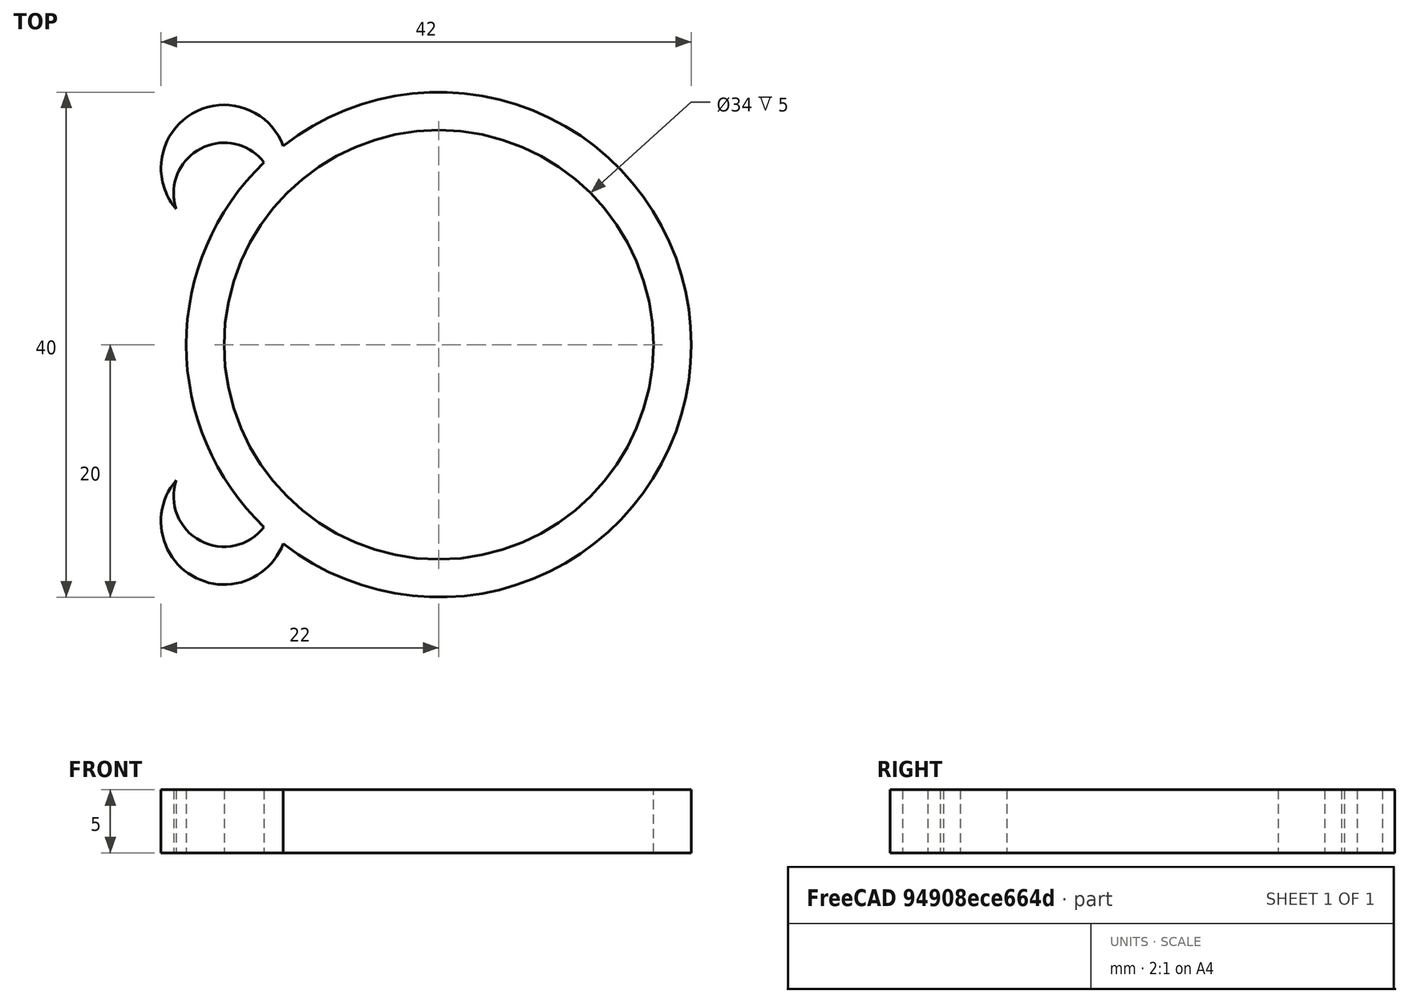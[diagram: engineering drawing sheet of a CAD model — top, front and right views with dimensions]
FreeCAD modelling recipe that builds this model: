
FCSTD DOCUMENT  (FreeCAD 0.20R29410 (Git))
Label: demon
License: Creative Commons Attribution
LicenseURL: http://creativecommons.org/licenses/by/4.0/
objects: Part::Cylinder×6, Part::Cut×3, Part::MultiFuse×2
note: 11 computed .brp shape members not serialized (recipe doc carries the construction recipe); baked Part::Feature solids carry a one-line shape summary decoded from their .brp

FEATURE [Part::Cylinder] Cylinder  label="Cilindro"
  Angle = 360
  AttacherType = Attacher::AttachEngine3D
  FirstAngle = 0
  Height = 5
  Radius = 20
  SecondAngle = 0
FEATURE [Part::Cylinder] Cylinder001  label="Cilindro001"
  Angle = 360
  AttacherType = Attacher::AttachEngine3D
  FirstAngle = 0
  Height = 5
  Radius = 17
  SecondAngle = 0
FEATURE [Part::Cut] Cut
  Base = -> Cylinder
  Refine = true
  Tool = -> Cylinder001
FEATURE [Part::Cylinder] Cylinder002  label="Cilindro002"
  Angle = 360
  AttacherType = Attacher::AttachEngine3D
  FirstAngle = 0
  Height = 5
  Radius = 5
  SecondAngle = 0
FEATURE [Part::Cylinder] Cylinder003  label="Cilindro003"
  Angle = 360
  AttacherType = Attacher::AttachEngine3D
  FirstAngle = 0
  Height = 5
  Placement = pos=(0,2,0) rot=(0,0,1;0rad)
  Radius = 4
  SecondAngle = 0
FEATURE [Part::Cut] Cut001
  Base = -> Cylinder002
  Placement = pos=(-17,-14,0) rot=(0,0,1;0rad)
  Refine = true
  Tool = -> Cylinder003
FEATURE [Part::Cylinder] Cylinder004  label="Cilindro004"
  Angle = 360
  AttacherType = Attacher::AttachEngine3D
  FirstAngle = 0
  Height = 5
  Radius = 5
  SecondAngle = 0
FEATURE [Part::Cylinder] Cylinder005  label="Cilindro005"
  Angle = 360
  AttacherType = Attacher::AttachEngine3D
  FirstAngle = 0
  Height = 5
  Placement = pos=(0,2,0) rot=(0,0,1;0rad)
  Radius = 4
  SecondAngle = 0
FEATURE [Part::Cut] Cut002
  Base = -> Cylinder004
  Placement = pos=(-17,14,0) rot=(0,0,-1;3.14159rad)
  Refine = true
  Tool = -> Cylinder005
FEATURE [Part::MultiFuse] Fusion
  Refine = true
  Shapes = -> [Cut,Cut001]
FEATURE [Part::MultiFuse] Fusion001
  Refine = true
  Shapes = -> [Cut002,Fusion]
